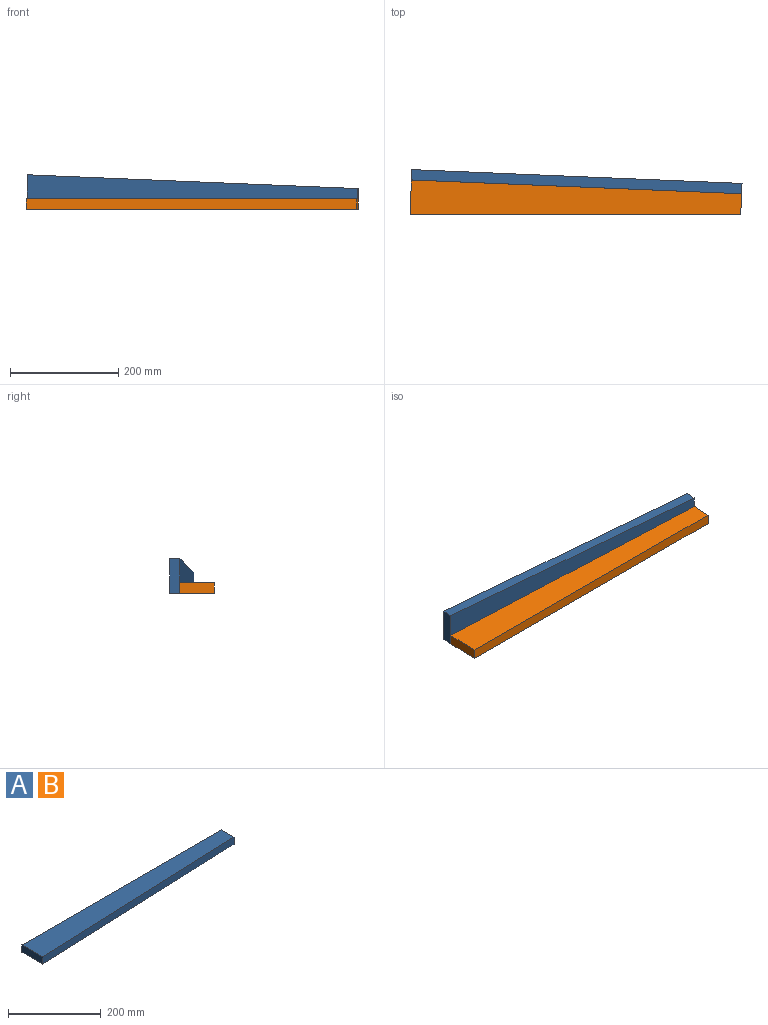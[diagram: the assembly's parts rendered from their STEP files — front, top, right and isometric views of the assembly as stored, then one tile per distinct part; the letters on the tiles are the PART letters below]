
ASSEMBLY  parts=2 mates=1
PART A: 6 faces, bbox 609.6x63.5x19.1 mm
  f0: plane 609.6x19.05mm, normal (0,1,0), area 11612.9mm2, adj f1,f3,f4,f5
  f1: plane 63.5x19.05mm, normal (-1,0,0), area 1209.7mm2, adj f0,f2,f4,f5
  f2: plane 609.6x25.4mm, normal (0.04,-1,0), area 11623mm2, adj f1,f3,f4,f5
  f3: plane 38.1x19.05mm, normal (1,0,0), area 725.8mm2, adj f0,f2,f4,f5
  f4: plane 609.6x63.5mm, normal (0,0,1), area 30967.7mm2, adj f0,f1,f2,f3
  f5: plane 609.6x63.5mm, normal (0,0,-1), area 30967.7mm2, adj f0,f1,f2,f3
PART B: same geometry as A
PLACE A rot(axis=(-1,0.02,-0.02),90deg) t=(-87.28,182.92,23.85)mm
PLACE B rot(axis=(0,0,-1),2.4deg) t=(-89.92,119.47,-39.65)mm fixed
MATE fastened A.f1 <-> B.f1  axis (-1,0.04,0) through (-87.28,182.92,-39.65)mm
